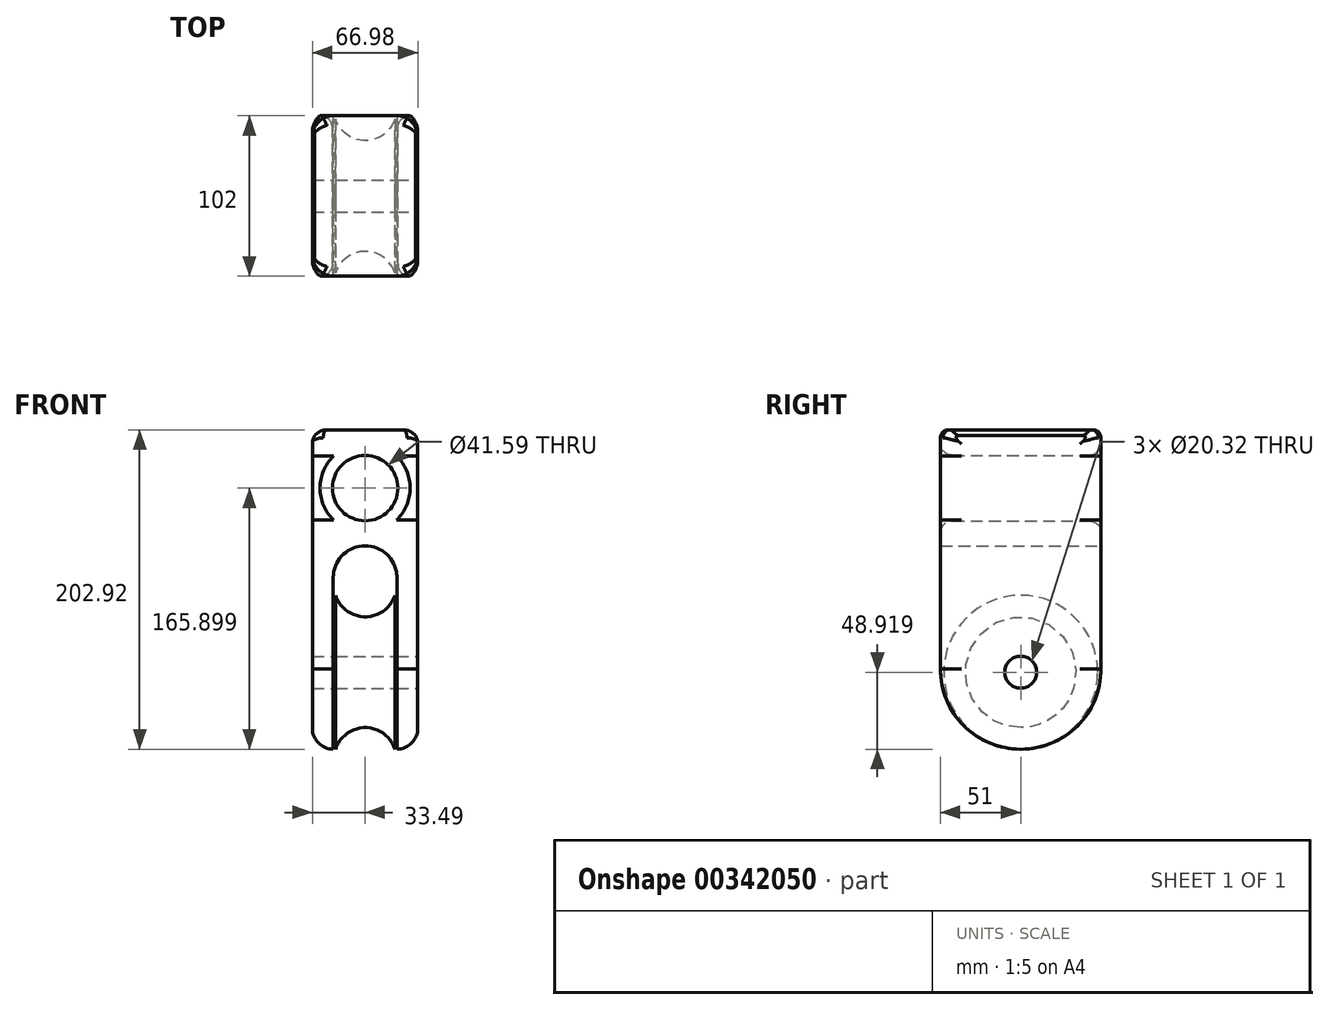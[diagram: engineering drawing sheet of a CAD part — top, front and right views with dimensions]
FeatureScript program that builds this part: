
annotation { "Feature Type Name" : "Feature", "Feature Type Description" : "" }
export const myFeature = defineFeature(function(context is Context, id is Id, definition is map)
    precondition{}
    {
        {
            var Q0;
            Q0=qCreatedBy(makeId("Front.planeOp"),FACE);
            var sketch = newSketch(context, id + "F0", { "sketchPlane" : qUnion([Q0])});
            skArc(sketch, "E0", {"start": v(-18.77, 0) * mm, "mid": v(0.1, -13.72) * mm, "end": v(18.95, 0) * mm});
            skLineSegment(sketch, "E1", {"start": v(18.95, 0) * mm, "end": v(18.95, -38.98) * mm});
            skLineSegment(sketch, "E2", {"start": v(-18.77, 0) * mm, "end": v(-18.77, -38.98) * mm});
            skLineSegment(sketch, "E3", {"start": v(-18.77, -38.98) * mm, "end": v(18.95, -38.98) * mm});
            skLineSegment(sketch, "E4", {"start": v(-32.66, -48.36) * mm, "end": v(34.46, -48.36) * mm, "construction": true});
            skSolve(sketch);
        }
        {
            var Q0;
            Q0=qCreatedBy(makeId("Front.planeOp"),FACE);
            var sketch = newSketch(context, id + "F1", { "sketchPlane" : qUnion([Q0])});
            skLineSegment(sketch, "E5", {"start": v(49.8, -48.9) * mm, "end": v(-47.28, -48.9) * mm, "construction": true});
            skSolve(sketch);
        }
        {
            var Q0;
            Q0 = qSketchRegion(id + "F0", true);
            var Q1;
            Q1=sQuery(id+"F1.wireOp",EDGE,"E5");
            revolve(context, id + "F2", {"entities" : qUnion([Q0]), "axis" : qUnion([Q1]), "revolveType" : RevolveType.FULL});
        }
        {
            var Q0;
            Q0=qCreatedBy(makeId("Front.planeOp"),FACE);
            var sketch = newSketch(context, id + "F3", { "sketchPlane" : qUnion([Q0])});
            skLineSegment(sketch, "E6", {"start": v(-20.22, -97.82) * mm, "end": v(-20.22, 11.16) * mm});
            skArc(sketch, "E7", {"start": v(-20.22, 11.16) * mm, "mid": v(-14.3, 25.45) * mm, "end": v(0, 31.37) * mm});
            skLineSegment(sketch, "E8", {"start": v(-20.22, -97.82) * mm, "end": v(-33.49, -97.82) * mm});
            skLineSegment(sketch, "E9", {"start": v(-33.49, -97.82) * mm, "end": v(-33.49, 99.34) * mm});
            skLineSegment(sketch, "E10", {"start": v(-33.49, 99.34) * mm, "end": v(-29.44, 105.1) * mm});
            skLineSegment(sketch, "E11", {"start": v(-29.44, 105.1) * mm, "end": v(0, 105.1) * mm});
            skArc(sketch, "E12.MirrorCS", {"start": v(20.22, 11.16) * mm, "mid": v(14.3, 25.45) * mm, "end": v(0, 31.37) * mm});
            skLineSegment(sketch, "E13.MirrorCS", {"start": v(20.22, -97.82) * mm, "end": v(20.22, 11.16) * mm});
            skLineSegment(sketch, "E14.MirrorCS", {"start": v(20.22, -97.82) * mm, "end": v(33.49, -97.82) * mm});
            skLineSegment(sketch, "E15.MirrorCS", {"start": v(33.49, -97.82) * mm, "end": v(33.49, 99.34) * mm});
            skLineSegment(sketch, "E16.MirrorCS", {"start": v(33.49, 99.34) * mm, "end": v(29.44, 105.1) * mm});
            skLineSegment(sketch, "E17.MirrorCS", {"start": v(29.44, 105.1) * mm, "end": v(0, 105.1) * mm});
            skCircle(sketch, "E18", {"center": v(0, 68.08) * mm, "radius": 20.8 * mm});
            skSolve(sketch);
        }
        {
            var Q0;
            Q0 = qSketchRegion(id + "F3", true);
            extrude(context, id + "F4", {"entities" : qUnion([Q0]), "endBound" : BoundingType.SYMMETRIC, "depth" : 102 * mm});
        }
        {
            var Q0;
            Q0=makeQuery(id+"F4.opExtrude","SWEPT_FACE",FACE,{"disambiguationData":[OSD([sQuery(id+"F3.wireOp",EDGE,"E15.MirrorCS")])]});
            var sketch = newSketch(context, id + "F5", { "sketchPlane" : qUnion([Q0])});
            skCircle(sketch, "E19", {"center": v(0, -48.9) * mm, "radius": 10.16 * mm});
            skSolve(sketch);
        }
        {
            var Q0;
            Q0 = qSketchRegion(id + "F5", true);
            extrude(context, id + "F6", {"entities" : qUnion([Q0]), "operationType" : NewBodyOperationType.REMOVE, "endBound" : BoundingType.THROUGH_ALL, "oppositeDirection" : true, "depth" : 25.4 * mm});
        }
        {
            var Q0;
            Q0=makeQuery(id+"F4.opExtrude","CAP_EDGE",EDGE,{"disambiguationData":[OSD([sQuery(id+"F3.wireOp",EDGE,"E18")])],"isStart":true});
            var Q1;
            Q1=makeQuery(id+"F4.opExtrude","CAP_EDGE",EDGE,{"disambiguationData":[OSD([sQuery(id+"F3.wireOp",EDGE,"E18")])],"isStart":false});
            fillet(context, id + "F7", {"entities" : qUnion([Q0, Q1]), "radius" : 7.8 * mm, "tangentPropagation" : true, "allowEdgeOverflow" : false});
        }
        {
            var Q0;
            Q0=makeQuery(id+"F4.opExtrude","CAP_EDGE",EDGE,{"disambiguationData":[OSD([sQuery(id+"F3.wireOp",EDGE,"E14.MirrorCS")])],"isStart":false});
            var Q1;
            Q1=makeQuery(id+"F4.opExtrude","CAP_EDGE",EDGE,{"disambiguationData":[OSD([sQuery(id+"F3.wireOp",EDGE,"E8")])],"isStart":false});
            var Q2;
            Q2=makeQuery(id+"F4.opExtrude","CAP_EDGE",EDGE,{"disambiguationData":[OSD([sQuery(id+"F3.wireOp",EDGE,"E8")])],"isStart":true});
            var Q3;
            Q3=makeQuery(id+"F4.opExtrude","CAP_EDGE",EDGE,{"disambiguationData":[OSD([sQuery(id+"F3.wireOp",EDGE,"E14.MirrorCS")])],"isStart":true});
            fillet(context, id + "F8", {"entities" : qUnion([Q0, Q1, Q2, Q3]), "radius" : 50.8 * mm, "tangentPropagation" : true, "allowEdgeOverflow" : false});
        }
        {
            var Q0;
            Q0=makeQuery(id+"F4.opExtrude","SWEPT_EDGE",EDGE,{"disambiguationData":[OSD([sQuery(id+"F3.wireOp",EDGE,"E15.MirrorCS"),sQuery(id+"F3.wireOp",EDGE,"E16.MirrorCS")])]});
            var Q1;
            Q1=makeQuery(id+"F4.opExtrude","SWEPT_EDGE",EDGE,{"disambiguationData":[OSD([sQuery(id+"F3.wireOp",EDGE,"E16.MirrorCS"),sQuery(id+"F3.wireOp",EDGE,"E17.MirrorCS")])]});
            var Q2;
            Q2=makeQuery(id+"F4.opExtrude","SWEPT_EDGE",EDGE,{"disambiguationData":[OSD([sQuery(id+"F3.wireOp",EDGE,"E10"),sQuery(id+"F3.wireOp",EDGE,"E11")])]});
            var Q3;
            Q3=makeQuery(id+"F4.opExtrude","SWEPT_EDGE",EDGE,{"disambiguationData":[OSD([sQuery(id+"F3.wireOp",EDGE,"E9"),sQuery(id+"F3.wireOp",EDGE,"E10")])]});
            fillet(context, id + "F9", {"entities" : qUnion([Q0, Q1, Q2, Q3]), "radius" : 10.22 * mm, "tangentPropagation" : true, "allowEdgeOverflow" : false});
        }
        {
            var Q0;
            Q0=makeQuery(id+"F4.opExtrude","CAP_EDGE",EDGE,{"disambiguationData":[OSD([sQuery(id+"F3.wireOp",EDGE,"E15.MirrorCS")])],"isStart":true});
            var Q1;
            Q1=makeQuery(id+"F4.opExtrude","CAP_EDGE",EDGE,{"disambiguationData":[OSD([sQuery(id+"F3.wireOp",EDGE,"E9")])],"isStart":true});
            fillet(context, id + "F10", {"entities" : qUnion([Q0, Q1]), "radius" : 13.35 * mm, "tangentPropagation" : true, "allowEdgeOverflow" : false});
        }
        {
            var Q0;
            Q0=makeQuery(id+"F10.opFillet","BLEND_EDGE",EDGE,{"blendedFrom":[makeQuery(id+"F4.opExtrude","CAP_EDGE",EDGE,{"disambiguationData":[OSD([sQuery(id+"F3.wireOp",EDGE,"E15.MirrorCS")])],"isStart":false}),makeQuery(id+"F9.opFillet","BLEND_FACE",FACE,{"disambiguationData":[OSD([sQuery(id+"F3.wireOp",EDGE,"E16.MirrorCS"),sQuery(id+"F3.wireOp",EDGE,"E17.MirrorCS")])]})],"blendedInto":[makeQuery(id+"F9.opFillet","BLEND_FACE",FACE,{"disambiguationData":[OSD([sQuery(id+"F3.wireOp",EDGE,"E16.MirrorCS"),sQuery(id+"F3.wireOp",EDGE,"E17.MirrorCS")])]})]});
            var Q1;
            Q1=makeQuery(id+"F4.opExtrude","CAP_EDGE",EDGE,{"disambiguationData":[OSD([sQuery(id+"F3.wireOp",EDGE,"E11"),sQuery(id+"F3.wireOp",EDGE,"E17.MirrorCS")])],"isStart":true});
            fillet(context, id + "F11", {"entities" : qUnion([Q0, Q1]), "radius" : 5.08 * mm, "tangentPropagation" : true, "allowEdgeOverflow" : false});
        }
    });
